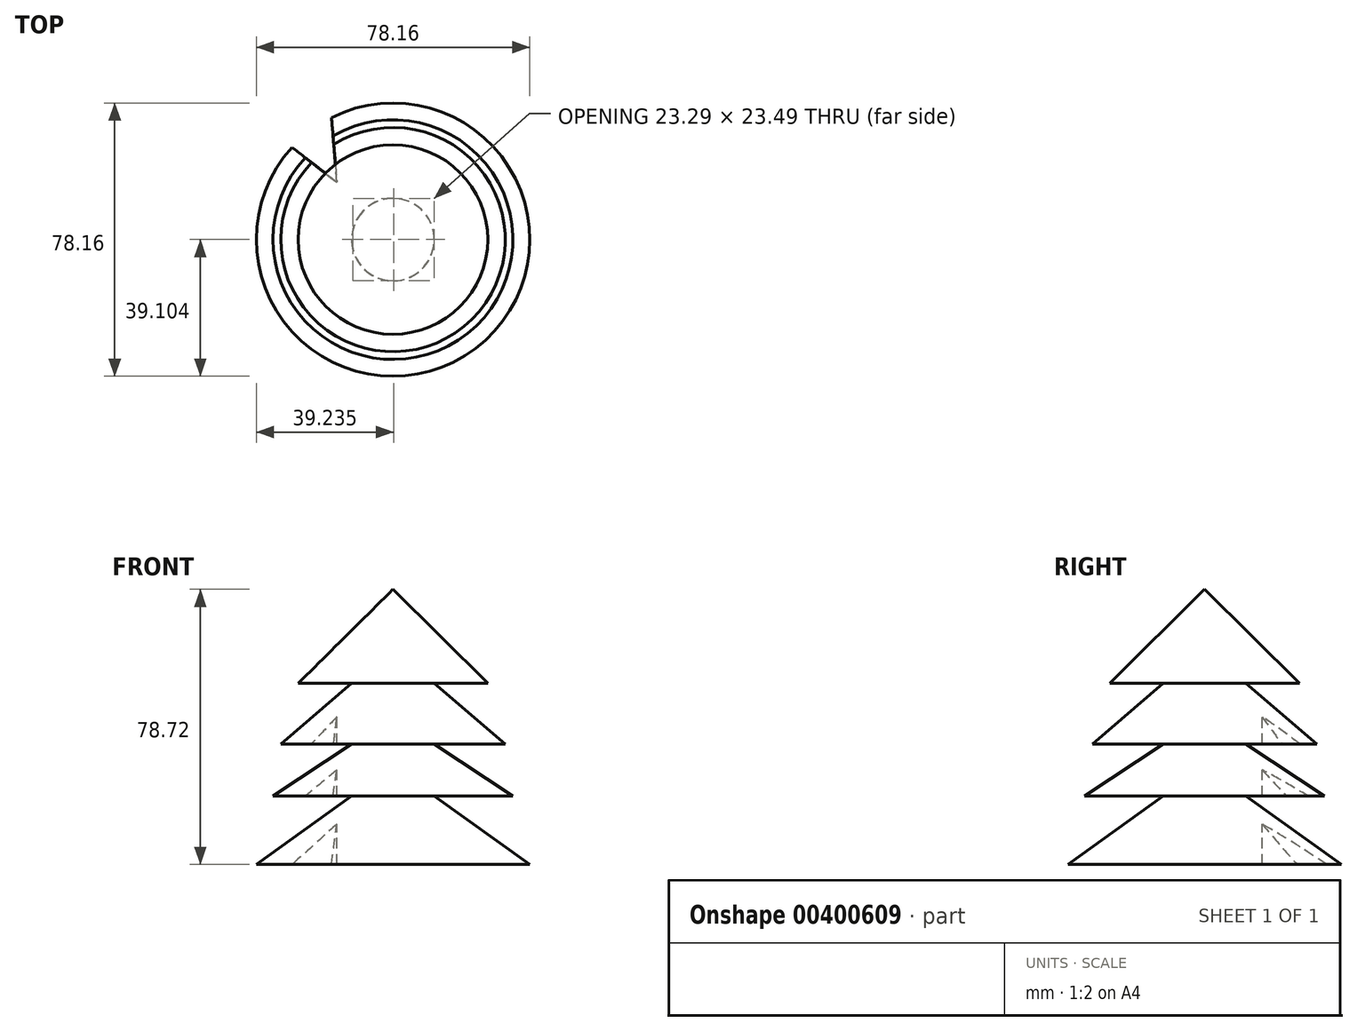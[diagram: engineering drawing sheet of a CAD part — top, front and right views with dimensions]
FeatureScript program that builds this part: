
annotation { "Feature Type Name" : "Feature", "Feature Type Description" : "" }
export const myFeature = defineFeature(function(context is Context, id is Id, definition is map)
    precondition{}
    {
        {
            var Q0;
            Q0=qCreatedBy(makeId("Front.planeOp"),FACE);
            var sketch = newSketch(context, id + "F0", { "sketchPlane" : qUnion([Q0])});
            skLineSegment(sketch, "E0", {"start": v(0, -42.59) * mm, "end": v(39.08, -42.59) * mm});
            skLineSegment(sketch, "E1", {"start": v(39.08, -42.59) * mm, "end": v(11.8, -23.04) * mm});
            skLineSegment(sketch, "E2", {"start": v(11.8, -23.04) * mm, "end": v(34.3, -23.04) * mm});
            skLineSegment(sketch, "E3", {"start": v(34.3, -23.04) * mm, "end": v(11.8, -8.11) * mm});
            skLineSegment(sketch, "E4", {"start": v(11.8, -8.11) * mm, "end": v(32.08, -8.11) * mm});
            skLineSegment(sketch, "E5", {"start": v(32.08, -8.11) * mm, "end": v(11.8, 9.22) * mm});
            skLineSegment(sketch, "E6", {"start": v(11.8, 9.22) * mm, "end": v(27.1, 9.22) * mm});
            skLineSegment(sketch, "E7", {"start": v(27.1, 9.22) * mm, "end": v(0, 36.13) * mm});
            skLineSegment(sketch, "E8", {"start": v(0, 36.13) * mm, "end": v(0, -44.06) * mm});
            skPoint(sketch, "E9.start.orphan", {"position": v(-23.78, 9.22) * mm});
            skPoint(sketch, "E10.start.orphan", {"position": v(-7.93, 9.22) * mm});
            skPoint(sketch, "E11.start.orphan", {"position": v(-28.76, -8.11) * mm});
            skPoint(sketch, "E12.start.orphan", {"position": v(-7.93, -8.11) * mm});
            skPoint(sketch, "E13.start.orphan", {"position": v(-32.08, -23.04) * mm});
            skPoint(sketch, "E14.start.orphan", {"position": v(-7.93, -23.04) * mm});
            skSolve(sketch);
        }
        {
            var Q0;
            {var subQ0=sQuery(id+"F0.wireOp",EDGE,"E0");Q0=makeQuery(id+"F0.imprint","IMPRINT",FACE,{"disambiguationData":[TD([[makeQuery(id+"F0.imprint","IMPRINT",EDGE,{"derivedFrom":subQ0}),1.0]])]});}
            var Q1;
            Q1=sQuery(id+"F0.wireOp",EDGE,"E8");
            revolve(context, id + "F1", {"entities" : qUnion([Q0]), "axis" : qUnion([Q1]), "revolveType" : RevolveType.FULL});
        }
        {
            var Q0;
            Q0=qCreatedBy(makeId("Top.planeOp"),FACE);
            var sketch = newSketch(context, id + "F2", { "sketchPlane" : qUnion([Q0])});
            skLineSegment(sketch, "E15", {"start": v(-33.55, 30.05) * mm, "end": v(-16.04, 16.4) * mm});
            skLineSegment(sketch, "E16", {"start": v(-16.04, 16.4) * mm, "end": v(-17.88, 38.53) * mm});
            skLineSegment(sketch, "E17", {"start": v(-17.88, 38.53) * mm, "end": v(-33.55, 30.05) * mm});
            skSolve(sketch);
        }
        {
            var Q0;
            Q0=makeQuery(id+"F2.imprint","IMPRINT",FACE,{"disambiguationData":[TD([[makeQuery(id+"F2.imprint","IMPRINT",EDGE,{"derivedFrom":sQuery(id+"F2.wireOp",EDGE,"E15")}),1.0]])]});
            extrude(context, id + "F3", {"entities" : qUnion([Q0]), "operationType" : NewBodyOperationType.REMOVE, "endBound" : BoundingType.THROUGH_ALL, "oppositeDirection" : true, "depth" : 25.4 * mm});
        }
    });
